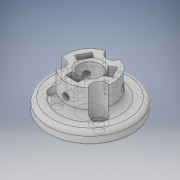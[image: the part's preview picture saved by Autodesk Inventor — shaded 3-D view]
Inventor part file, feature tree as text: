
AUTODESK INVENTOR PART (.ipt)
format: ipt  version: 2019 (Build 230136000, 136)  size: 298,496 bytes
history: native  units: mm
features: sketch x6, extrude x4, fillet x4, hole x2, plane x1, pattern_circular x1
ambient origin geometry x8: Origin, YZ Plane, XZ Plane, XY Plane, X Axis, Y Axis, Z Axis, Center Point
bodies: Solid1 (feature_tree)
feature tree (18):
  extrude  "Extrusion1"  Depth=6.0mm TaperAngle=0.0deg
  extrude  "Extrusion2"  Depth=12.0mm TaperAngle=0.0deg
  hole  "Hole1"  [1 undecoded]
  hole  "Hole2"  [1 undecoded]
  plane  "Work Plane1"
  extrude  "Extrusion3"  Depth=1.0mm TaperAngle=0.0deg
  extrude  "Extrusion4"  Depth=1.0mm
  fillet  "Fillet1"  Radius=3.25mm
  fillet  "Fillet2"  Radius=1.0mm
  pattern_circular  "Circular Pattern1"  [2 undecoded]
  fillet  "Fillet3"  Radius=30.0mm
  fillet  "Fillet4"  Radius=2.0mm
  sketch  "Sketch1"  dims[d0=40.0mm d1=6.0mm d2=0.0mm]
  sketch  "Sketch2"  dims[d3=23.0mm d4=12.0mm d5=0.0mm]
  sketch  "Sketch3"  dims[d6=23.0mm d7=60.0mm d9=360.0deg]
  sketch  "Sketch4"  dims[d11=4.0mm d12=6.0mm d13=7.0mm d14=15.0mm d15=90.0deg d16=8.0mm d17=90.0deg]
  sketch  "Sketch7"  dims[d18=10.25mm d19=6.0mm d20=7.0mm d21=13.0mm d22=90.0deg d23=8.0mm d24=90.0deg d25=7.25mm]
  sketch  "Sketch8"  dims[d27=6.0mm d28=3.0mm d29=0.0mm d30=3.1mm d31=3.25mm d32=4.25mm d33=0.0mm d34=0.0mm d35=1.0mm d36=3.0mm d37=30.0mm d38=360.0deg d40=2.0mm d41=1.0mm]
note: 4 required parameter values undecoded (feature->parameter linkage not recoverable at this tier; creation-order binding heuristic only, values carry confidence <= 0.55)
